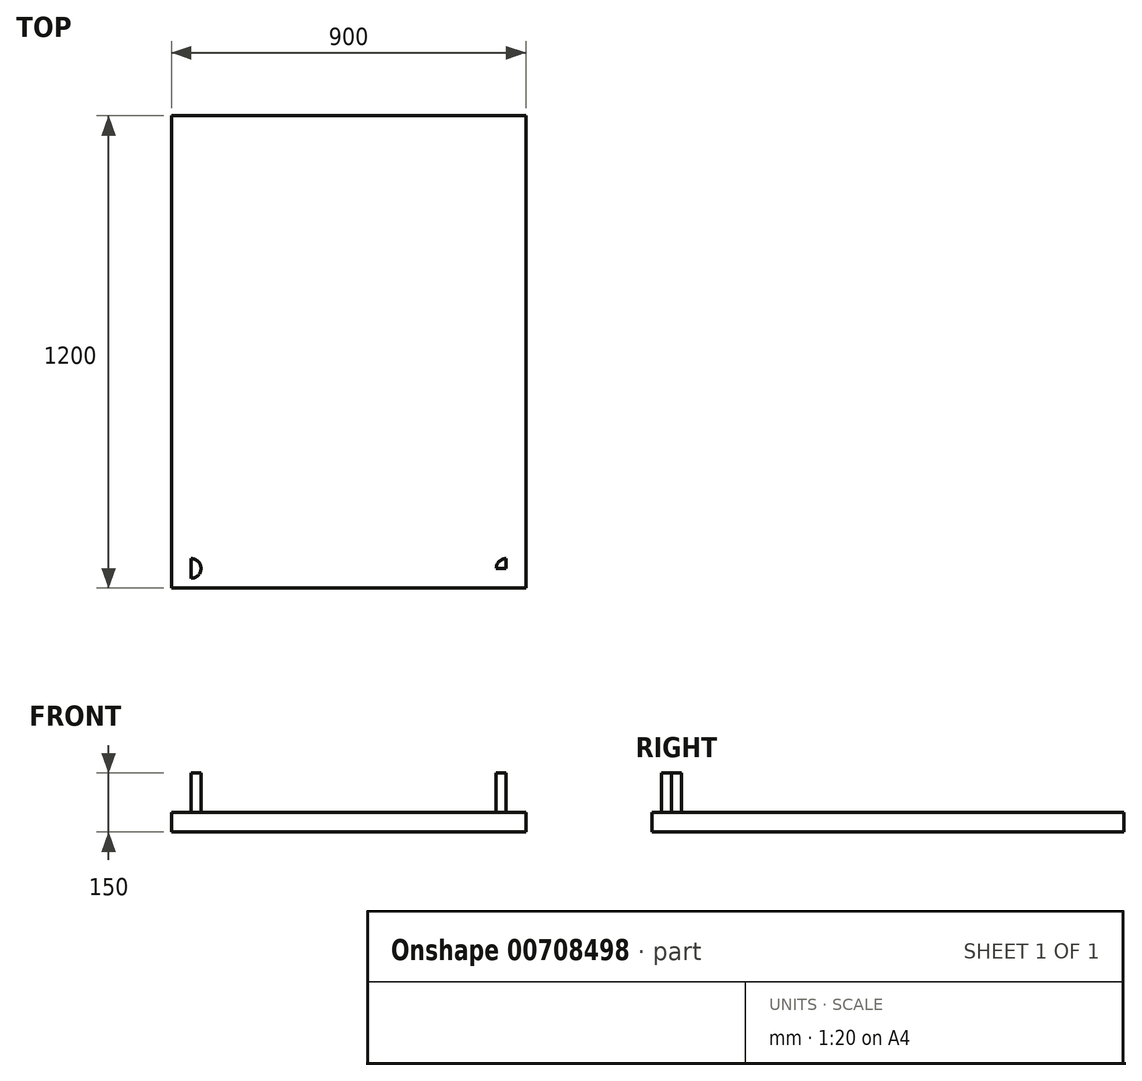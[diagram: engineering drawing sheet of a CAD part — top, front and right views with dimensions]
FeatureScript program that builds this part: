
annotation { "Feature Type Name" : "Feature", "Feature Type Description" : "" }
export const myFeature = defineFeature(function(context is Context, id is Id, definition is map)
    precondition{}
    {
        {
            var Q0;
            Q0=qCreatedBy(makeId("Top.planeOp"),FACE);
            var sketch = newSketch(context, id + "F0", { "sketchPlane" : qUnion([Q0])});
            skLineSegment(sketch, "E0.bottom", {"start": v(-450, -600) * mm, "end": v(450, -600) * mm});
            skLineSegment(sketch, "E0.top", {"start": v(-450, 600) * mm, "end": v(450, 600) * mm});
            skLineSegment(sketch, "E0.left", {"start": v(-450, -600) * mm, "end": v(-450, 600) * mm});
            skLineSegment(sketch, "E0.right", {"start": v(450, -600) * mm, "end": v(450, 600) * mm});
            skPoint(sketch, "E0.middle", {"position": v(0, 0) * mm});
            skSolve(sketch);
        }
        {
            var Q0;
            Q0=makeQuery(id+"F0.imprint","IMPRINT",FACE,{"disambiguationData":[TD([[makeQuery(id+"F0.imprint","IMPRINT",EDGE,{"derivedFrom":sQuery(id+"F0.wireOp",EDGE,"E0.bottom")}),1.0]])]});
            extrude(context, id + "F1", {"entities" : qUnion([Q0]), "depth" : -50 * mm, "offsetDistance" : 25 * mm});
        }
        {
            var Q0;
            Q0=makeQuery(id+"F0.imprint","IMPRINT",FACE,{"disambiguationData":[TD([[makeQuery(id+"F0.imprint","IMPRINT",EDGE,{"derivedFrom":sQuery(id+"F0.wireOp",EDGE,"E0.bottom")}),1.0]])]});
            var sketch = newSketch(context, id + "F2", { "sketchPlane" : qUnion([Q0])});
            skLineSegment(sketch, "E1.0", {"start": v(-400, -600) * mm, "end": v(-400, 600) * mm});
            skLineSegment(sketch, "E2.0", {"start": v(-450, 550) * mm, "end": v(450, 550) * mm});
            skLineSegment(sketch, "E3.0", {"start": v(400, -600) * mm, "end": v(400, 600) * mm});
            skLineSegment(sketch, "E4.0", {"start": v(-450, -550) * mm, "end": v(450, -550) * mm});
            skCircle(sketch, "E5", {"center": v(-400, -550) * mm, "radius": 25 * mm});
            skCircle(sketch, "E6", {"center": v(400, -550) * mm, "radius": 25 * mm});
            skSolve(sketch);
        }
        {
            var Q0;
            {var subQ0=sQuery(id+"F2.wireOp",EDGE,"E4.0");var subQ1=sQuery(id+"F2.wireOp",EDGE,"E1.0");var subQ2=makeQuery(id+"F2.imprint","INTERSECT",VERTEX,{"derivedFrom":[subQ1,subQ0]});Q0=makeQuery(id+"F2.imprint","IMPRINT",FACE,{"disambiguationData":[TD([[makeQuery(id+"F2.imprint","IMPRINT",EDGE,{"disambiguationData":[TD([[subQ2,-1.0]])],"derivedFrom":subQ1}),-1.0]])]});}
            var Q1;
            {var subQ0=sQuery(id+"F2.wireOp",EDGE,"E5");var subQ9=sQuery(id+"F2.wireOp",EDGE,"E1.0");var subQ11=makeQuery(id+"F2.imprint","INTERSECT",VERTEX,{"disambiguationData":[OD(1.0)],"derivedFrom":[subQ9,subQ0]});Q1=makeQuery(id+"F2.imprint","IMPRINT",FACE,{"disambiguationData":[TD([[makeQuery(id+"F2.imprint","IMPRINT",EDGE,{"disambiguationData":[TD([[subQ11,-1.0]])],"derivedFrom":subQ9}),-1.0]])]});}
            var Q2;
            {var subQ0=sQuery(id+"F2.wireOp",EDGE,"E4.0");var subQ1=sQuery(id+"F2.wireOp",EDGE,"E3.0");var subQ2=makeQuery(id+"F2.imprint","INTERSECT",VERTEX,{"derivedFrom":[subQ1,subQ0]});Q2=makeQuery(id+"F2.imprint","IMPRINT",FACE,{"disambiguationData":[TD([[makeQuery(id+"F2.imprint","IMPRINT",EDGE,{"disambiguationData":[TD([[subQ2,-1.0]])],"derivedFrom":subQ1}),1.0]])]});}
            extrude(context, id + "F3", {"entities" : qUnion([Q0, Q1, Q2]), "operationType" : NewBodyOperationType.ADD, "depth" : 100 * mm, "offsetDistance" : 25 * mm});
        }
        {
            var Q0;
            Q0=makeQuery(id+"F3.opExtrude","SWEPT_FACE",FACE,{"disambiguationData":[OSD([sQuery(id+"F2.wireOp",EDGE,"E4.0")])]});
            var sketch = newSketch(context, id + "F4", { "sketchPlane" : qUnion([Q0])});
            skFitSpline(sketch, "E7", {"points": [v(-400, 0) * mm, v(-394.05, 85.97) * mm, v(-339.08, 100) * mm, v(23.25, 100) * mm, v(343.97, 100) * mm, v(387.42, 89.43) * mm, v(400, 0) * mm], "startDerivative": vector(87.97, 676.3) * mm, "endDerivative": vector(161.23, -670.71) * mm});
            skSolve(sketch);
        }
        {
            var Q0;
            Q0=makeQuery(id+"F0.imprint","IMPRINT",FACE,{"disambiguationData":[TD([[makeQuery(id+"F0.imprint","IMPRINT",EDGE,{"derivedFrom":sQuery(id+"F0.wireOp",EDGE,"E0.bottom")}),1.0]])]});
            var sketch = newSketch(context, id + "F5", { "sketchPlane" : qUnion([Q0])});
            skCircle(sketch, "E8", {"center": v(-400.05, -549.93) * mm, "radius": 25 * mm});
            skCircle(sketch, "E9", {"center": v(400.22, -550.42) * mm, "radius": 25 * mm});
            skSolve(sketch);
        }
        {
            var Q0;
            Q0=makeQuery(id+"F5.imprint","IMPRINT",FACE,{"disambiguationData":[TD([[makeQuery(id+"F5.imprint","IMPRINT",EDGE,{"derivedFrom":sQuery(id+"F5.wireOp",EDGE,"E8")}),-1.0]])]});
            var Q1;
            Q1=sQuery(id+"F5.wireOp",EDGE,"E8");
            var Q2;
            Q2=sQuery(id+"F4.wireOp",EDGE,"E7");
            sweep(context, id + "F6", {"bodyType" : ToolBodyType.SURFACE, "profiles" : qUnion([Q0]), "surfaceProfiles" : qUnion([Q1]), "path" : qUnion([Q2])});
        }
    });
